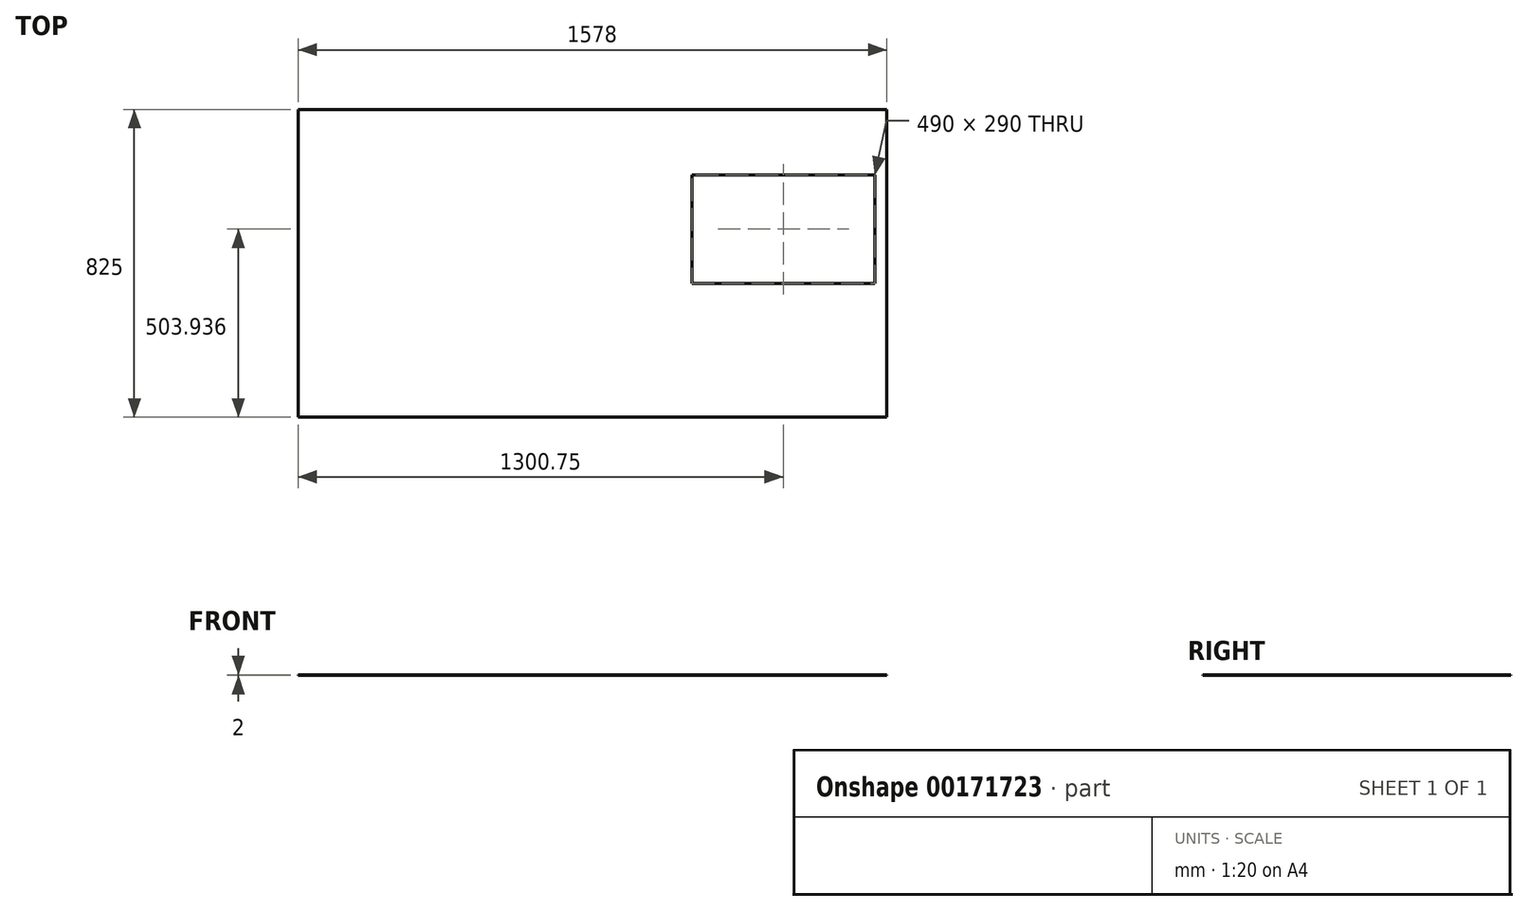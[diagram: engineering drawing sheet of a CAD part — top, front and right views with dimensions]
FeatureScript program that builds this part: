
annotation { "Feature Type Name" : "Feature", "Feature Type Description" : "" }
export const myFeature = defineFeature(function(context is Context, id is Id, definition is map)
    precondition{}
    {
        {
            var Q0;
            Q0=qCreatedBy(makeId("Top.planeOp"),FACE);
            var sketch = newSketch(context, id + "F0", { "sketchPlane" : qUnion([Q0])});
            skLineSegment(sketch, "E0.bottom", {"start": v(-789, 412.5) * mm, "end": v(789, 412.5) * mm});
            skLineSegment(sketch, "E0.top", {"start": v(-789, -412.5) * mm, "end": v(789, -412.5) * mm});
            skLineSegment(sketch, "E0.left", {"start": v(-789, 412.5) * mm, "end": v(-789, -412.5) * mm});
            skLineSegment(sketch, "E0.right", {"start": v(789, 412.5) * mm, "end": v(789, -412.5) * mm});
            skPoint(sketch, "E0.middle", {"position": v(0, 0) * mm});
            skLineSegment(sketch, "E1.bottom", {"start": v(756.75, 236.44) * mm, "end": v(266.75, 236.44) * mm});
            skLineSegment(sketch, "E1.top", {"start": v(756.75, -53.56) * mm, "end": v(266.75, -53.56) * mm});
            skLineSegment(sketch, "E1.left", {"start": v(756.75, 236.44) * mm, "end": v(756.75, -53.56) * mm});
            skLineSegment(sketch, "E1.right", {"start": v(266.75, 236.44) * mm, "end": v(266.75, -53.56) * mm});
            skSolve(sketch);
        }
        {
            var Q0;
            Q0 = qSketchRegion(id + "F0", true);
            var Q1;
            Q1=makeQuery(id+"F0.imprint","IMPRINT",FACE,{"disambiguationData":[TD([[makeQuery(id+"F0.imprint","IMPRINT",EDGE,{"derivedFrom":sQuery(id+"F0.wireOp",EDGE,"E0.bottom")}),-1.0]])]});
            extrude(context, id + "F1", {"entities" : qUnion([Q0, Q1]), "depth" : 2 * mm});
        }
    });
